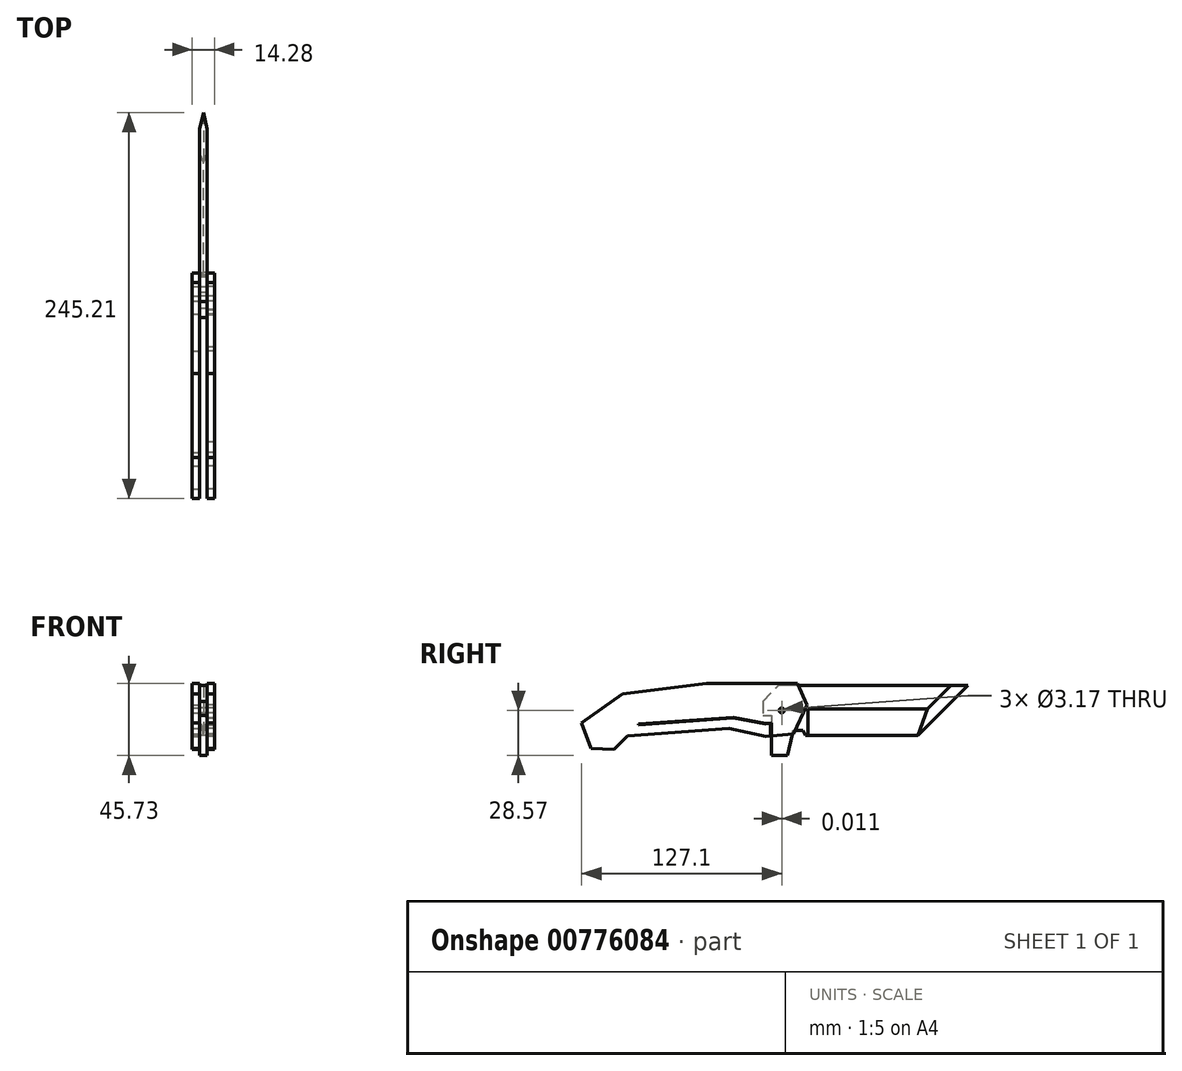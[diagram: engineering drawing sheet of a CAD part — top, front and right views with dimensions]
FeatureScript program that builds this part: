
annotation { "Feature Type Name" : "Feature", "Feature Type Description" : "" }
export const myFeature = defineFeature(function(context is Context, id is Id, definition is map)
    precondition{}
    {
        {
            var Q0;
            Q0=qCreatedBy(makeId("Right.planeOp"),FACE);
            var sketch = newSketch(context, id + "F0", { "sketchPlane" : qUnion([Q0])});
            skLineSegment(sketch, "E0.bottom", {"start": v(50.8, 15.88) * mm, "end": v(-50.8, 15.88) * mm});
            skLineSegment(sketch, "E0.top", {"start": v(50.8, -15.88) * mm, "end": v(-50.8, -15.88) * mm});
            skLineSegment(sketch, "E0.left", {"start": v(50.8, 15.88) * mm, "end": v(50.8, -15.88) * mm});
            skLineSegment(sketch, "E0.right", {"start": v(-50.8, 15.88) * mm, "end": v(-50.8, -15.88) * mm});
            skPoint(sketch, "E0.middle", {"position": v(0, 0) * mm});
            skSolve(sketch);
        }
        {
            var Q0;
            Q0=qSketchRegion(id+"F0",true);
            extrude(context, id + "F1", {"entities" : qUnion([Q0]), "endBound" : BoundingType.SYMMETRIC, "oppositeDirection" : true, "depth" : 4.76 * mm, "offsetDistance" : 25.4 * mm});
        }
        {
            var Q0;
            Q0=makeQuery(id+"F1.opExtrude","SWEPT_FACE",FACE,{"disambiguationData":[OSD([sQuery(id+"F0.wireOp",EDGE,"E0.left")])]});
            var sketch = newSketch(context, id + "F2", { "sketchPlane" : qUnion([Q0])});
            skLineSegment(sketch, "E1", {"start": v(0, -15.87) * mm, "end": v(-2.38, 1.07) * mm});
            skLineSegment(sketch, "E2", {"start": v(0, -15.87) * mm, "end": v(0, -2.24) * mm, "construction": true});
            skLineSegment(sketch, "E3", {"start": v(0, -15.88) * mm, "end": v(2.38, 1.07) * mm});
            skLineSegment(sketch, "E4", {"start": v(-2.38, 1.07) * mm, "end": v(-18.49, 1.07) * mm});
            skLineSegment(sketch, "E5", {"start": v(-18.49, 1.07) * mm, "end": v(-18.49, -23.62) * mm});
            skLineSegment(sketch, "E6", {"start": v(-18.49, -23.62) * mm, "end": v(17.54, -23.62) * mm});
            skLineSegment(sketch, "E7", {"start": v(17.54, -23.62) * mm, "end": v(17.54, 1.07) * mm});
            skLineSegment(sketch, "E8", {"start": v(17.54, 1.07) * mm, "end": v(2.38, 1.07) * mm});
            skSolve(sketch);
        }
        {
            var Q0;
            Q0=qSketchRegion(id+"F2",true);
            extrude(context, id + "F3", {"entities" : qUnion([Q0]), "operationType" : NewBodyOperationType.REMOVE, "endBound" : BoundingType.THROUGH_ALL, "oppositeDirection" : true, "depth" : 25.4 * mm, "offsetDistance" : 25.4 * mm});
        }
        {
            var Q0;
            Q0=qCreatedBy(makeId("Right.planeOp"),FACE);
            var sketch = newSketch(context, id + "F4", { "sketchPlane" : qUnion([Q0])});
            skLineSegment(sketch, "E9", {"start": v(50.8, 15.88) * mm, "end": v(19.05, -15.88) * mm});
            skSolve(sketch);
        }
        {
            var Q0;
            Q0=makeQuery(id+"F1.opExtrude","SWEPT_FACE",FACE,{"disambiguationData":[OSD([sQuery(id+"F0.wireOp",EDGE,"E0.bottom")])]});
            var sketch = newSketch(context, id + "F5", { "sketchPlane" : qUnion([Q0])});
            skLineSegment(sketch, "E10", {"start": v(0, 50.8) * mm, "end": v(2.38, 40.06) * mm});
            skLineSegment(sketch, "E11", {"start": v(0, 50.8) * mm, "end": v(-2.38, 40.06) * mm});
            skLineSegment(sketch, "E12", {"start": v(2.38, 40.06) * mm, "end": v(25.29, 40.06) * mm});
            skLineSegment(sketch, "E13", {"start": v(25.29, 40.06) * mm, "end": v(21.97, 103.42) * mm});
            skLineSegment(sketch, "E14", {"start": v(21.97, 103.42) * mm, "end": v(-23.8, 103.42) * mm});
            skLineSegment(sketch, "E15", {"start": v(-23.8, 103.42) * mm, "end": v(-27.67, 37.97) * mm});
            skLineSegment(sketch, "E16", {"start": v(-27.67, 37.97) * mm, "end": v(-2.38, 40.06) * mm});
            skSolve(sketch);
        }
        {
            var Q0;
            Q0=qSketchRegion(id+"F5",true);
            var Q1;
            Q1=qSketchRegion(id+"F4",true);
            var Q2;
            Q2=qConstructionFilter(qBodyType(qCreatedBy(id+"F4",EDGE),BodyType.WIRE),ConstructionObject.NO);
            sweep(context, id + "F6", {"operationType" : NewBodyOperationType.REMOVE, "profiles" : qUnion([Q0, Q1]), "path" : qUnion([Q2])});
        }
        {
            var Q0;
            Q0=qCreatedBy(makeId("Right.planeOp"),FACE);
            var sketch = newSketch(context, id + "F7", { "sketchPlane" : qUnion([Q0])});
            skLineSegment(sketch, "E17", {"start": v(-50.8, -15.87) * mm, "end": v(-52.39, -15.87) * mm});
            skLineSegment(sketch, "E18", {"start": v(-50.8, 15.88) * mm, "end": v(-79.38, 15.87) * mm});
            skLineSegment(sketch, "E19", {"start": v(-79.38, 15.87) * mm, "end": v(-79.38, -3.17) * mm});
            skLineSegment(sketch, "E20", {"start": v(-79.38, -3.18) * mm, "end": v(-73.85, -3.18) * mm});
            skLineSegment(sketch, "E21", {"start": v(-73.85, -3.18) * mm, "end": v(-73.85, -28.58) * mm});
            skLineSegment(sketch, "E22", {"start": v(-73.85, -28.58) * mm, "end": v(-63.69, -28.58) * mm});
            skLineSegment(sketch, "E23", {"start": v(-63.69, -28.58) * mm, "end": v(-60.04, -12.7) * mm});
            skLineSegment(sketch, "E24", {"start": v(-60.04, -12.7) * mm, "end": v(-53.69, -12.7) * mm});
            skLineSegment(sketch, "E25", {"start": v(-53.69, -12.7) * mm, "end": v(-52.39, -15.87) * mm});
            skLineSegment(sketch, "E26", {"start": v(-50.8, 15.88) * mm, "end": v(-50.8, -15.87) * mm});
            skCircle(sketch, "E27", {"center": v(-67.31, 0) * mm, "radius": 1.59 * mm});
            skSolve(sketch);
        }
        {
            var Q0;
            Q0=qSketchRegion(id+"F7",true);
            extrude(context, id + "F8", {"entities" : qUnion([Q0]), "operationType" : NewBodyOperationType.ADD, "endBound" : BoundingType.SYMMETRIC, "depth" : 4.76 * mm, "offsetDistance" : 25.4 * mm});
        }
        {
            var Q0;
            Q0=makeQuery(id+"F8.opExtrude","SWEPT_EDGE",EDGE,{"disambiguationData":[OSD([sQuery(id+"F7.wireOp",EDGE,"E18"),sQuery(id+"F7.wireOp",EDGE,"E19")])]});
            chamfer(context, id + "F9", {"entities" : qUnion([Q0]), "width" : 10.16 * mm, "tangentPropagation" : true});
        }
        {
            var Q0;
            Q0=makeQuery(id+"F8.boolean.opBoolean","MERGE",FACE,{"derivedFrom":[makeQuery(id+"F1.opExtrude","CAP_FACE",FACE,{"disambiguationData":[OSD([sQuery(id+"F0.wireOp",EDGE,"E0.bottom"),sQuery(id+"F0.wireOp",EDGE,"E0.top"),sQuery(id+"F0.wireOp",EDGE,"E0.left"),sQuery(id+"F0.wireOp",EDGE,"E0.right")])],"isStart":true}),makeQuery(id+"F8.opExtrude","CAP_FACE",FACE,{"disambiguationData":[OSD([sQuery(id+"F7.wireOp",EDGE,"E17"),sQuery(id+"F7.wireOp",EDGE,"E18"),sQuery(id+"F7.wireOp",EDGE,"E19"),sQuery(id+"F7.wireOp",EDGE,"E20"),sQuery(id+"F7.wireOp",EDGE,"E21"),sQuery(id+"F7.wireOp",EDGE,"E22"),sQuery(id+"F7.wireOp",EDGE,"E23"),sQuery(id+"F7.wireOp",EDGE,"E24"),sQuery(id+"F7.wireOp",EDGE,"E25"),sQuery(id+"F7.wireOp",EDGE,"E26"),sQuery(id+"F7.wireOp",EDGE,"E27")])],"isStart":false})]});
            var sketch = newSketch(context, id + "F10", { "sketchPlane" : qUnion([Q0])});
            skCircle(sketch, "E28", {"center": v(-67.31, 0) * mm, "radius": 15.88 * mm, "construction": true});
            skSolve(sketch);
        }
        {
            var Q0;
            {var subQ8=sQuery(id+"F7.wireOp",EDGE,"E17");Q0=makeQuery(id+"F10.imprint","IMPRINT",FACE,{"disambiguationData":[TD([[makeQuery(id+"F10.imprint","IMPRINT",EDGE,{"derivedFrom":makeQuery(id+"F8.opExtrude","CAP_EDGE",EDGE,{"disambiguationData":[OSD([subQ8])],"isStart":false})}),-1.0]])]});}
            var sketch = newSketch(context, id + "F11", { "sketchPlane" : qUnion([Q0])});
            skLineSegment(sketch, "E29", {"start": v(-115.05, 17.16) * mm, "end": v(-57.22, 17.16) * mm});
            skLineSegment(sketch, "E30", {"start": v(-57.22, 17.16) * mm, "end": v(-51.23, 3.41) * mm});
            skLineSegment(sketch, "E31", {"start": v(-51.23, 3.41) * mm, "end": v(-59.74, -14.96) * mm});
            skLineSegment(sketch, "E32", {"start": v(-59.74, -14.96) * mm, "end": v(-77.17, -16.54) * mm});
            skLineSegment(sketch, "E33", {"start": v(-77.17, -16.54) * mm, "end": v(-100.87, -11.45) * mm});
            skLineSegment(sketch, "E34", {"start": v(-100.87, -11.45) * mm, "end": v(-165.33, -16.07) * mm});
            skPoint(sketch, "E34.endSnap0", {"position": v(-89.02, -14) * mm});
            skLineSegment(sketch, "E35", {"start": v(-165.33, -16.07) * mm, "end": v(-173.7, -24.81) * mm});
            skLineSegment(sketch, "E36", {"start": v(-188.34, -24.23) * mm, "end": v(-173.7, -24.81) * mm});
            skLineSegment(sketch, "E37", {"start": v(-188.34, -24.23) * mm, "end": v(-194.41, -8) * mm});
            skLineSegment(sketch, "E38", {"start": v(-194.41, -8) * mm, "end": v(-168.37, 10.54) * mm});
            skLineSegment(sketch, "E39", {"start": v(-168.37, 10.54) * mm, "end": v(-115.05, 17.16) * mm});
            skCircle(sketch, "E40", {"center": v(-67.3, 0) * mm, "radius": 1.59 * mm});
            skSolve(sketch);
        }
        {
            var Q0;
            Q0=qSketchRegion(id+"F11",true);
            extrude(context, id + "F12", {"entities" : qUnion([Q0]), "depth" : 4.76 * mm, "offsetDistance" : 25.4 * mm});
        }
        {
            var Q0;
            Q0=makeQuery(id+"F12.opExtrude","SWEPT_BODY",BODY,{"disambiguationData":[OSD([sQuery(id+"F11.wireOp",EDGE,"E29"),sQuery(id+"F11.wireOp",EDGE,"E30"),sQuery(id+"F11.wireOp",EDGE,"E31"),sQuery(id+"F11.wireOp",EDGE,"E32"),sQuery(id+"F11.wireOp",EDGE,"E33"),sQuery(id+"F11.wireOp",EDGE,"E34"),sQuery(id+"F11.wireOp",EDGE,"E35"),sQuery(id+"F11.wireOp",EDGE,"E36"),sQuery(id+"F11.wireOp",EDGE,"E37"),sQuery(id+"F11.wireOp",EDGE,"E38"),sQuery(id+"F11.wireOp",EDGE,"E39"),sQuery(id+"F11.wireOp",EDGE,"E40")])]});
            var Q1;
            Q1=qCreatedBy(makeId("Right.planeOp"),FACE);
            mirror(context, id + "F13", {"entities" : qUnion([Q0]), "mirrorPlane" : qUnion([Q1])});
        }
        {
            var Q0;
            Q0=makeQuery(id+"F12.opExtrude","CAP_FACE",FACE,{"disambiguationData":[OSD([sQuery(id+"F11.wireOp",EDGE,"E29"),sQuery(id+"F11.wireOp",EDGE,"E30"),sQuery(id+"F11.wireOp",EDGE,"E31"),sQuery(id+"F11.wireOp",EDGE,"E32"),sQuery(id+"F11.wireOp",EDGE,"E33"),sQuery(id+"F11.wireOp",EDGE,"E34"),sQuery(id+"F11.wireOp",EDGE,"E35"),sQuery(id+"F11.wireOp",EDGE,"E36"),sQuery(id+"F11.wireOp",EDGE,"E37"),sQuery(id+"F11.wireOp",EDGE,"E38"),sQuery(id+"F11.wireOp",EDGE,"E39"),sQuery(id+"F11.wireOp",EDGE,"E40")])],"isStart":false});
            var sketch = newSketch(context, id + "F14", { "sketchPlane" : qUnion([Q0])});
            skLineSegment(sketch, "E41", {"start": v(-74.5, -16.3) * mm, "end": v(-74.5, -8.36) * mm});
            skLineSegment(sketch, "E42", {"start": v(-98.06, -4.89) * mm, "end": v(-158.23, -9.2) * mm});
            skLineSegment(sketch, "E43.0", {"start": v(-98.03, -4.37) * mm, "end": v(-158.28, -8.7) * mm});
            skLineSegment(sketch, "E43.2", {"start": v(-73.98, -16.25) * mm, "end": v(-73.98, -7.8) * mm});
            skLineSegment(sketch, "E44", {"start": v(-158.23, -9.2) * mm, "end": v(-158.28, -8.7) * mm});
            skLineSegment(sketch, "E45", {"start": v(-74.5, -16.3) * mm, "end": v(-73.98, -16.25) * mm});
            skLineSegment(sketch, "E46", {"start": v(-98.06, -4.89) * mm, "end": v(-77.56, -8.64) * mm});
            skLineSegment(sketch, "E47", {"start": v(-77.56, -8.64) * mm, "end": v(-74.5, -8.36) * mm});
            skLineSegment(sketch, "E48.0", {"start": v(-77.53, -8.13) * mm, "end": v(-73.98, -7.8) * mm});
            skLineSegment(sketch, "E48.1", {"start": v(-98.03, -4.37) * mm, "end": v(-77.53, -8.13) * mm});
            skSolve(sketch);
        }
        {
            var Q0;
            Q0=qSketchRegion(id+"F14",true);
            var Q1;
            Q1=makeQuery(id+"F1.opExtrude","SWEPT_BODY",BODY,{"disambiguationData":[OSD([sQuery(id+"F0.wireOp",EDGE,"E0.bottom"),sQuery(id+"F0.wireOp",EDGE,"E0.top"),sQuery(id+"F0.wireOp",EDGE,"E0.left"),sQuery(id+"F0.wireOp",EDGE,"E0.right")])]});
            extrude(context, id + "F15", {"entities" : qUnion([Q0]), "operationType" : NewBodyOperationType.REMOVE, "endBound" : BoundingType.UP_TO_NEXT, "oppositeDirection" : true, "depth" : 25.4 * mm, "endBoundEntityBody" : qUnion([Q1]), "offsetDistance" : 25.4 * mm});
        }
    });
